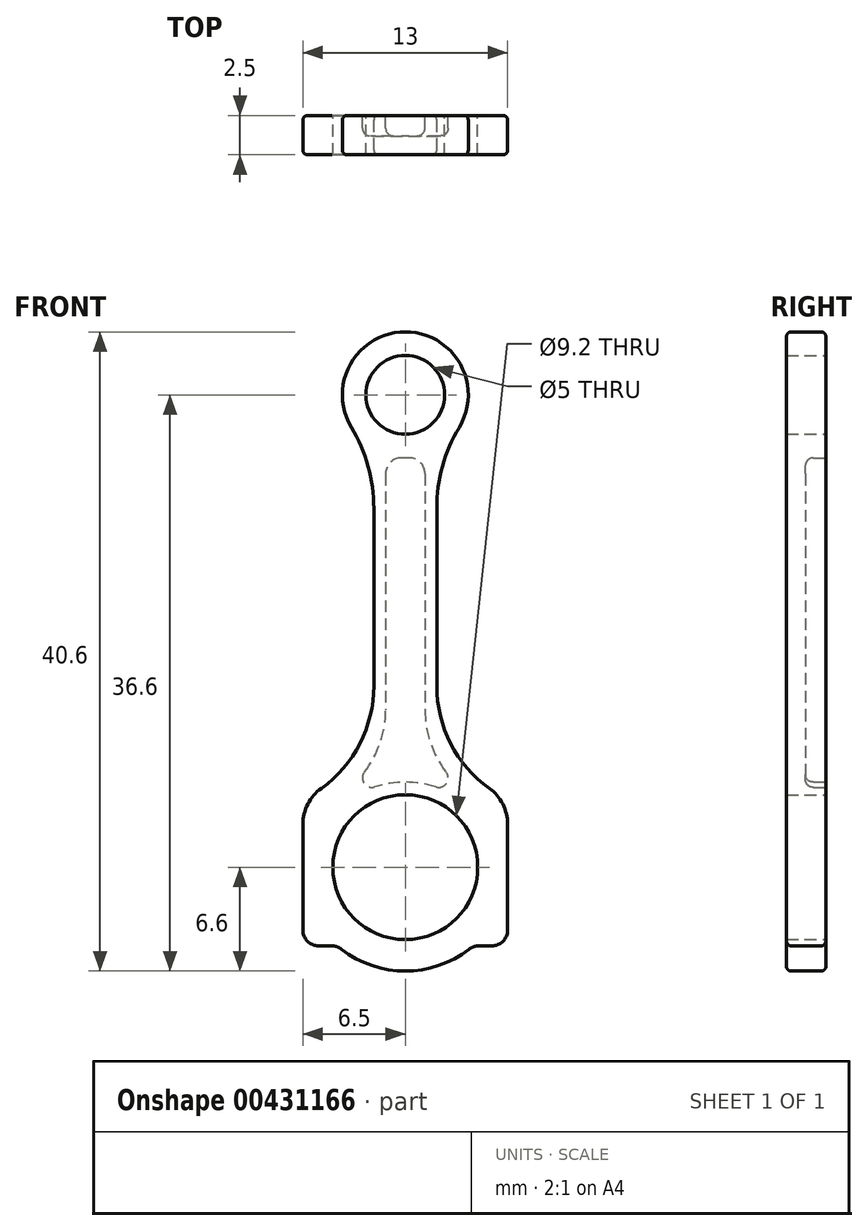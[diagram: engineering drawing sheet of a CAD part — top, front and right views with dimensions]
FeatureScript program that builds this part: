
annotation { "Feature Type Name" : "Feature", "Feature Type Description" : "" }
export const myFeature = defineFeature(function(context is Context, id is Id, definition is map)
    precondition{}
    {
        {
            var Q0;
            Q0=qCreatedBy(makeId("Front.planeOp"),FACE);
            var sketch = newSketch(context, id + "F0", { "sketchPlane" : qUnion([Q0])});
            skCircle(sketch, "E0", {"center": v(0, 0) * mm, "radius": 4.6 * mm});
            skArc(sketch, "E1", {"start": v(-4.3, -5) * mm, "mid": v(0, -6.6) * mm, "end": v(4.3, -5) * mm});
            skLineSegment(sketch, "E2.left", {"start": v(-2, 11.5) * mm, "end": v(-2, 22.79) * mm});
            skLineSegment(sketch, "E2.right", {"start": v(2, 11.5) * mm, "end": v(2, 22.79) * mm});
            skLineSegment(sketch, "E3", {"start": v(0, 0) * mm, "end": v(0, 54.19) * mm, "construction": true});
            skCircle(sketch, "E4", {"center": v(0, 30) * mm, "radius": 2.5 * mm});
            skCircle(sketch, "E5", {"center": v(0, 30) * mm, "radius": 4 * mm});
            skArc(sketch, "E6", {"start": v(-2, 22.79) * mm, "mid": v(-2.36, 25.46) * mm, "end": v(-3.43, 27.94) * mm});
            skArc(sketch, "E7", {"start": v(3.43, 27.94) * mm, "mid": v(2.36, 25.46) * mm, "end": v(2, 22.79) * mm});
            skLineSegment(sketch, "E8", {"start": v(-4.3, -5) * mm, "end": v(-6.5, -5) * mm});
            skLineSegment(sketch, "E9", {"start": v(-6.5, -5) * mm, "end": v(-6.5, 2.73) * mm});
            skLineSegment(sketch, "E10", {"start": v(4.3, -5) * mm, "end": v(6.5, -5) * mm});
            skLineSegment(sketch, "E11", {"start": v(6.5, -5) * mm, "end": v(6.5, 2.73) * mm});
            skArc(sketch, "E12", {"start": v(-5.33, 5) * mm, "mid": v(-6.2, 4.01) * mm, "end": v(-6.5, 2.73) * mm});
            skArc(sketch, "E13", {"start": v(-5.33, 5) * mm, "mid": v(-2.88, 7.85) * mm, "end": v(-2, 11.5) * mm});
            skArc(sketch, "E14", {"start": v(2, 11.5) * mm, "mid": v(2.88, 7.85) * mm, "end": v(5.33, 5) * mm});
            skArc(sketch, "E15", {"start": v(6.5, 2.73) * mm, "mid": v(6.2, 4.01) * mm, "end": v(5.33, 5) * mm});
            skSolve(sketch);
        }
        {
            var Q0;
            Q0=makeQuery(id+"F0.imprint","IMPRINT",FACE,{"disambiguationData":[TD([[makeQuery(id+"F0.imprint","IMPRINT",EDGE,{"derivedFrom":sQuery(id+"F0.wireOp",EDGE,"E0")}),-1.0]])]});
            var Q1;
            Q1=makeQuery(id+"F0.imprint","IMPRINT",FACE,{"disambiguationData":[TD([[makeQuery(id+"F0.imprint","IMPRINT",EDGE,{"derivedFrom":sQuery(id+"F0.wireOp",EDGE,"E4")}),-1.0]])]});
            extrude(context, id + "F1", {"entities" : qUnion([Q0, Q1]), "depth" : 2.5 * mm});
        }
        {
            var Q0;
            Q0=makeQuery(id+"F1.opExtrude","CAP_FACE",FACE,{"disambiguationData":[OSD([sQuery(id+"F0.wireOp",EDGE,"E0"),sQuery(id+"F0.wireOp",EDGE,"E1"),sQuery(id+"F0.wireOp",EDGE,"E2.left"),sQuery(id+"F0.wireOp",EDGE,"E2.right"),sQuery(id+"F0.wireOp",EDGE,"E4"),sQuery(id+"F0.wireOp",EDGE,"E5"),sQuery(id+"F0.wireOp",EDGE,"E6"),sQuery(id+"F0.wireOp",EDGE,"E7"),sQuery(id+"F0.wireOp",EDGE,"E8"),sQuery(id+"F0.wireOp",EDGE,"E9"),sQuery(id+"F0.wireOp",EDGE,"E10"),sQuery(id+"F0.wireOp",EDGE,"E11"),sQuery(id+"F0.wireOp",EDGE,"E12"),sQuery(id+"F0.wireOp",EDGE,"E13"),sQuery(id+"F0.wireOp",EDGE,"E14"),sQuery(id+"F0.wireOp",EDGE,"E15")])],"isStart":true});
            var sketch = newSketch(context, id + "F2", { "sketchPlane" : qUnion([Q0])});
            skLineSegment(sketch, "E16.bottom", {"start": v(-1.25, 26) * mm, "end": v(1.25, 26) * mm});
            skLineSegment(sketch, "E16.left", {"start": v(-1.25, 26) * mm, "end": v(-1.25, 10) * mm});
            skLineSegment(sketch, "E16.right", {"start": v(1.25, 26) * mm, "end": v(1.25, 10) * mm});
            skLineSegment(sketch, "E17", {"start": v(0, 0) * mm, "end": v(0, 44.11) * mm, "construction": true});
            skArc(sketch, "E18", {"start": v(0, 5.4) * mm, "mid": v(-0.98, 5.32) * mm, "end": v(-1.94, 5.1) * mm});
            skArc(sketch, "E19", {"start": v(-2.6, 6.04) * mm, "mid": v(-2.61, 5.33) * mm, "end": v(-1.94, 5.1) * mm});
            skArc(sketch, "E20", {"start": v(-2.6, 6.04) * mm, "mid": v(-1.6, 7.9) * mm, "end": v(-1.25, 10) * mm});
            skArc(sketch, "E21.MirrorCS", {"start": v(0, 5.4) * mm, "mid": v(0.98, 5.32) * mm, "end": v(1.94, 5.1) * mm});
            skArc(sketch, "E22.MirrorCS", {"start": v(2.6, 6.04) * mm, "mid": v(2.61, 5.33) * mm, "end": v(1.94, 5.1) * mm});
            skArc(sketch, "E23.MirrorCS", {"start": v(2.6, 6.04) * mm, "mid": v(1.6, 7.9) * mm, "end": v(1.25, 10) * mm});
            skSolve(sketch);
        }
        {
            var Q0;
            Q0=makeQuery(id+"F2.imprint","IMPRINT",FACE,{"disambiguationData":[TD([[makeQuery(id+"F2.imprint","IMPRINT",EDGE,{"derivedFrom":sQuery(id+"F2.wireOp",EDGE,"E16.bottom")}),-1.0]])]});
            extrude(context, id + "F3", {"entities" : qUnion([Q0]), "operationType" : NewBodyOperationType.REMOVE, "oppositeDirection" : true, "depth" : 1.3 * mm});
        }
        {
            var Q0;
            Q0=makeQuery(id+"F3.boolean.opBoolean","COPY",EDGE,{"derivedFrom":makeQuery(id+"F3.opExtrude","SWEPT_EDGE",EDGE,{"disambiguationData":[OSD([sQuery(id+"F2.wireOp",EDGE,"E16.bottom"),sQuery(id+"F2.wireOp",EDGE,"E16.left")])]})});
            var Q1;
            Q1=makeQuery(id+"F3.boolean.opBoolean","COPY",EDGE,{"derivedFrom":makeQuery(id+"F3.opExtrude","SWEPT_EDGE",EDGE,{"disambiguationData":[OSD([sQuery(id+"F2.wireOp",EDGE,"E16.bottom"),sQuery(id+"F2.wireOp",EDGE,"E16.right")])]})});
            var Q2;
            Q2=makeQuery(id+"F3.boolean.opBoolean","COPY",EDGE,{"derivedFrom":makeQuery(id+"F3.opExtrude","SWEPT_EDGE",EDGE,{"disambiguationData":[OSD([sQuery(id+"F2.wireOp",EDGE,"E16.top"),sQuery(id+"F2.wireOp",EDGE,"E16.left")])]})});
            var Q3;
            Q3=makeQuery(id+"F3.boolean.opBoolean","COPY",EDGE,{"derivedFrom":makeQuery(id+"F3.opExtrude","SWEPT_EDGE",EDGE,{"disambiguationData":[OSD([sQuery(id+"F2.wireOp",EDGE,"E16.top"),sQuery(id+"F2.wireOp",EDGE,"E16.right")])]})});
            fillet(context, id + "F4", {"entities" : qUnion([Q0, Q1, Q2, Q3]), "radius" : 1 * mm, "tangentPropagation" : true, "allowEdgeOverflow" : false});
        }
        {
            var Q0;
            Q0=makeQuery(id+"F1.opExtrude","SWEPT_EDGE",EDGE,{"disambiguationData":[OSD([sQuery(id+"F0.wireOp",EDGE,"E1"),sQuery(id+"F0.wireOp",EDGE,"E10")])]});
            var Q1;
            Q1=makeQuery(id+"F1.opExtrude","SWEPT_EDGE",EDGE,{"disambiguationData":[OSD([sQuery(id+"F0.wireOp",EDGE,"E10"),sQuery(id+"F0.wireOp",EDGE,"E11")])]});
            var Q2;
            Q2=makeQuery(id+"F1.opExtrude","SWEPT_EDGE",EDGE,{"disambiguationData":[OSD([sQuery(id+"F0.wireOp",EDGE,"E1"),sQuery(id+"F0.wireOp",EDGE,"E8")])]});
            var Q3;
            Q3=makeQuery(id+"F1.opExtrude","SWEPT_EDGE",EDGE,{"disambiguationData":[OSD([sQuery(id+"F0.wireOp",EDGE,"E8"),sQuery(id+"F0.wireOp",EDGE,"E9")])]});
            fillet(context, id + "F5", {"entities" : qUnion([Q0, Q1, Q2, Q3]), "radius" : 1 * mm, "tangentPropagation" : true, "allowEdgeOverflow" : false});
        }
        {
            var Q0;
            Q0=makeQuery(id+"F3.boolean.opBoolean","COPY",EDGE,{"derivedFrom":makeQuery(id+"F3.opExtrude","CAP_EDGE",EDGE,{"disambiguationData":[OSD([sQuery(id+"F2.wireOp",EDGE,"E18"),sQuery(id+"F2.wireOp",EDGE,"E21.MirrorCS")])],"isStart":false})});
            fillet(context, id + "F6", {"entities" : qUnion([Q0]), "radius" : 0.5 * mm, "tangentPropagation" : true, "allowEdgeOverflow" : false});
        }
        {
            var Q0;
            Q0=makeQuery(id+"F3.boolean.opBoolean","COPY",EDGE,{"derivedFrom":makeQuery(id+"F3.opExtrude","CAP_EDGE",EDGE,{"disambiguationData":[OSD([sQuery(id+"F2.wireOp",EDGE,"E19")])],"isStart":true})});
            var Q1;
            Q1=makeQuery(id+"F1.opExtrude","CAP_EDGE",EDGE,{"disambiguationData":[OSD([sQuery(id+"F0.wireOp",EDGE,"E11")])],"isStart":true});
            var Q2;
            Q2=makeQuery(id+"F1.opExtrude","CAP_EDGE",EDGE,{"disambiguationData":[OSD([sQuery(id+"F0.wireOp",EDGE,"E14")])],"isStart":false});
            fillet(context, id + "F7", {"entities" : qUnion([Q0, Q1, Q2]), "radius" : 0.3 * mm, "tangentPropagation" : true, "allowEdgeOverflow" : false});
        }
    });
